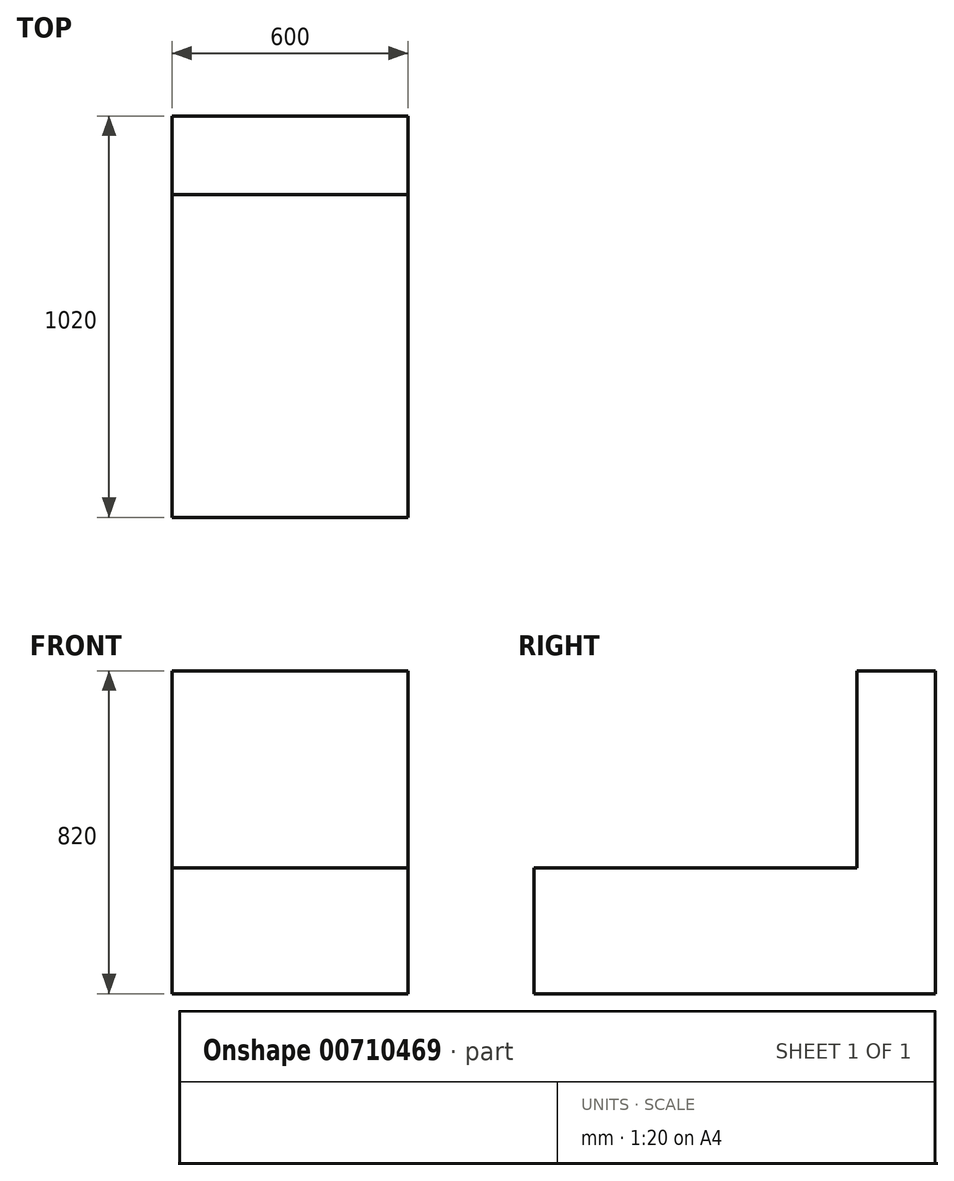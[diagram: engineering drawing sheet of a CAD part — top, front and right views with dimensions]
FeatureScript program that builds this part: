
annotation { "Feature Type Name" : "Feature", "Feature Type Description" : "" }
export const myFeature = defineFeature(function(context is Context, id is Id, definition is map)
    precondition{}
    {
        {
            var Q0;
            Q0=qCreatedBy(makeId("Top.planeOp"),FACE);
            var sketch = newSketch(context, id + "F0", { "sketchPlane" : qUnion([Q0])});
            skLineSegment(sketch, "E0.bottom", {"start": v(300, 510) * mm, "end": v(-300, 510) * mm});
            skLineSegment(sketch, "E0.top", {"start": v(300, -510) * mm, "end": v(-300, -510) * mm});
            skLineSegment(sketch, "E0.left", {"start": v(300, 510) * mm, "end": v(300, -510) * mm});
            skLineSegment(sketch, "E0.right", {"start": v(-300, 510) * mm, "end": v(-300, -510) * mm});
            skPoint(sketch, "E0.middle", {"position": v(0, 0) * mm});
            skSolve(sketch);
        }
        {
            var Q0;
            Q0=makeQuery(id+"F0.imprint","IMPRINT",FACE,{"disambiguationData":[TD([[makeQuery(id+"F0.imprint","IMPRINT",EDGE,{"derivedFrom":sQuery(id+"F0.wireOp",EDGE,"E0.bottom")}),1.0]])]});
            extrude(context, id + "F1", {"entities" : qUnion([Q0]), "depth" : 820 * mm, "offsetDistance" : 25 * mm});
        }
        {
            var Q0;
            Q0=makeQuery(id+"F1.opExtrude","CAP_FACE",FACE,{"disambiguationData":[OSD([sQuery(id+"F0.wireOp",EDGE,"E0.bottom"),sQuery(id+"F0.wireOp",EDGE,"E0.top"),sQuery(id+"F0.wireOp",EDGE,"E0.left"),sQuery(id+"F0.wireOp",EDGE,"E0.right")])],"isStart":false});
            var sketch = newSketch(context, id + "F2", { "sketchPlane" : qUnion([Q0])});
            skLineSegment(sketch, "E1.bottom", {"start": v(-300, -510) * mm, "end": v(300, -510) * mm});
            skLineSegment(sketch, "E1.top", {"start": v(-300, 310) * mm, "end": v(300, 310) * mm});
            skLineSegment(sketch, "E1.left", {"start": v(-300, -510) * mm, "end": v(-300, 310) * mm});
            skLineSegment(sketch, "E1.right", {"start": v(300, -510) * mm, "end": v(300, 310) * mm});
            skSolve(sketch);
        }
        {
            var Q0;
            Q0 = qSketchRegion(id + "F2", true);
            var Q1;
            Q1 = qConstructionFilter(qBodyType(qCreatedBy(id + "F2" ,EDGE), BodyType.WIRE), ConstructionObject.NO);
            extrude(context, id + "F3", {"entities" : qUnion([Q0]), "operationType" : NewBodyOperationType.REMOVE, "surfaceEntities" : qUnion([Q1]), "oppositeDirection" : true, "depth" : 500 * mm, "offsetDistance" : 25 * mm});
        }
    });
